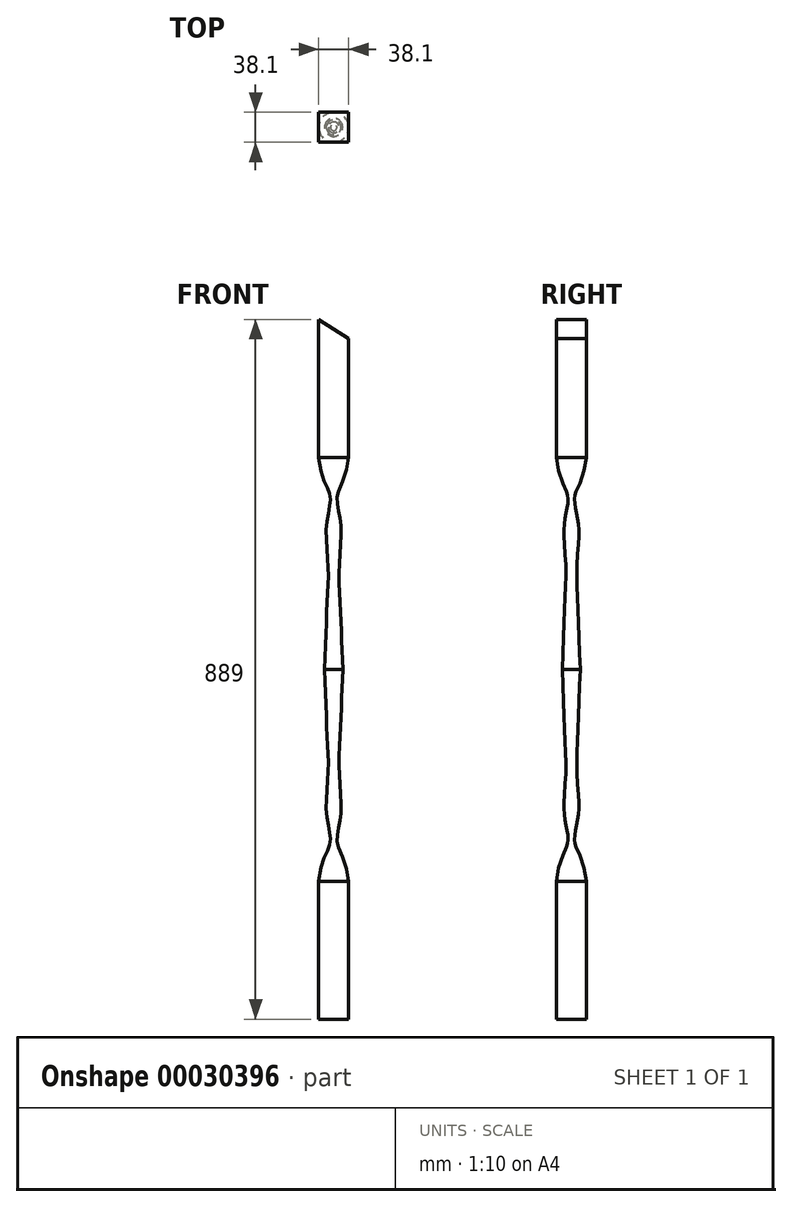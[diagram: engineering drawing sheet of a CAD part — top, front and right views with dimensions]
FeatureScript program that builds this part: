
annotation { "Feature Type Name" : "Feature", "Feature Type Description" : "" }
export const myFeature = defineFeature(function(context is Context, id is Id, definition is map)
    precondition{}
    {
        {
            var Q0;
            Q0=qCreatedBy(makeId("Top.planeOp"),FACE);
            var sketch = newSketch(context, id + "F0", { "sketchPlane" : qUnion([Q0])});
            skLineSegment(sketch, "E0.rect.bottom", {"start": v(19.05, 19.05) * mm, "end": v(-19.05, 19.05) * mm});
            skLineSegment(sketch, "E0.rect.top", {"start": v(19.05, -19.05) * mm, "end": v(-19.05, -19.05) * mm});
            skLineSegment(sketch, "E0.rect.left", {"start": v(19.05, 19.05) * mm, "end": v(19.05, -19.05) * mm});
            skLineSegment(sketch, "E0.rect.right", {"start": v(-19.05, 19.05) * mm, "end": v(-19.05, -19.05) * mm});
            skPoint(sketch, "E0.rect.middle", {"position": v(0, 0) * mm});
            skSolve(sketch);
        }
        {
            var Q0;
            Q0 = qSketchRegion(id + "F0", true);
            extrude(context, id + "F1", {"entities" : qUnion([Q0]), "endBound" : BoundingType.SYMMETRIC, "depth" : 889 * mm});
        }
        {
            var Q0;
            Q0=qCreatedBy(makeId("Front.planeOp"),FACE);
            var sketch = newSketch(context, id + "F2", { "sketchPlane" : qUnion([Q0])});
            skLineSegment(sketch, "E1", {"start": v(0, 0) * mm, "end": v(19.05, 0) * mm, "construction": true});
            skFitSpline(sketch, "E2", {"points": [v(11.55, 0) * mm, v(8.45, 81.36) * mm, v(7.05, 130.76) * mm, v(8.91, 185.4) * mm, v(4.34, 219.07) * mm, v(19.05, 269.25) * mm], "startDerivative": vector(-18.28, 345.8) * mm, "endDerivative": vector(55.06, 468.7) * mm});
            skLineSegment(sketch, "E3", {"start": v(0, 444.5) * mm, "end": v(0, -444.5) * mm, "construction": true});
            skFitSpline(sketch, "E4.MirrorCS", {"points": [v(11.55, 0) * mm, v(8.45, -81.36) * mm, v(7.05, -130.76) * mm, v(8.91, -185.4) * mm, v(4.34, -219.07) * mm, v(19.05, -269.25) * mm], "startDerivative": vector(-18.28, -345.8) * mm, "endDerivative": vector(55.06, -468.7) * mm});
            skLineSegment(sketch, "E5", {"start": v(19.05, -269.25) * mm, "end": v(67.7, -269.25) * mm});
            skLineSegment(sketch, "E6", {"start": v(67.7, -269.25) * mm, "end": v(67.7, 269.25) * mm});
            skLineSegment(sketch, "E7", {"start": v(19.05, 269.25) * mm, "end": v(67.7, 269.25) * mm});
            skSolve(sketch);
        }
        {
            var Q0;
            Q0 = qSketchRegion(id + "F2", true);
            var Q1;
            Q1=sQuery(id+"F2.wireOp",EDGE,"E3");
            revolve(context, id + "F3", {"operationType" : NewBodyOperationType.REMOVE, "entities" : qUnion([Q0]), "axis" : qUnion([Q1]), "revolveType" : RevolveType.FULL, "oppositeDirection" : true});
        }
        {
            var Q0;
            Q0=qCreatedBy(makeId("Front.planeOp"),FACE);
            var sketch = newSketch(context, id + "F4", { "sketchPlane" : qUnion([Q0])});
            skLineSegment(sketch, "E8", {"start": v(-19.05, 444.5) * mm, "end": v(19.05, 420.47) * mm});
            skLineSegment(sketch, "E9", {"start": v(-19.05, 444.5) * mm, "end": v(19.05, 444.5) * mm});
            skLineSegment(sketch, "E10", {"start": v(19.05, 444.5) * mm, "end": v(19.05, 420.47) * mm});
            skSolve(sketch);
        }
        {
            var Q0;
            Q0 = qSketchRegion(id + "F4", true);
            extrude(context, id + "F5", {"entities" : qUnion([Q0]), "operationType" : NewBodyOperationType.REMOVE, "endBound" : BoundingType.THROUGH_ALL, "oppositeDirection" : true, "depth" : 25.4 * mm, "hasSecondDirection" : true, "secondDirectionBound" : SecondDirectionBoundingType.THROUGH_ALL, "secondDirectionOppositeDirection" : false, "secondDirectionDepth" : 25.4 * mm});
        }
    });
